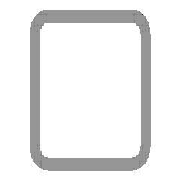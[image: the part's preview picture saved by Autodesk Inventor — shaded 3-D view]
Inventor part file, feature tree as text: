
AUTODESK INVENTOR PART (.ipt)
format: ipt  version: 2025.3 (Build 293356030, 356C)  size: 134,144 bytes
history: native  units: mm (DEFAULTED — no unit token found)
features: other x4, sketch x1, plane x1
ambient origin geometry x8: Origin, YZ Plane, XZ Plane, XY Plane, X Axis, Y Axis, Z Axis, Center Point
bodies: Solid1 (feature_tree), Body (feature_tree)
feature tree (6):
  parser-record x1  (decoder bookkeeping rows leaked as tree rows — omitted from the tree; the rows remain in map.json)
  other  "Driven Length"
  other  "Start Plane"
  other  "End Plane"
  sketch  "Sketch3"  dims[d3=260.0mm d4=0.0mm d7=4.0mm d9=40.0mm d11=40.0mm d12=2.0mm d13=40.0mm d14=300.0mm d15=20.0mm d16=20.0mm d17=90.0deg d18=260.0mm]
  plane  "Work Plane3"
